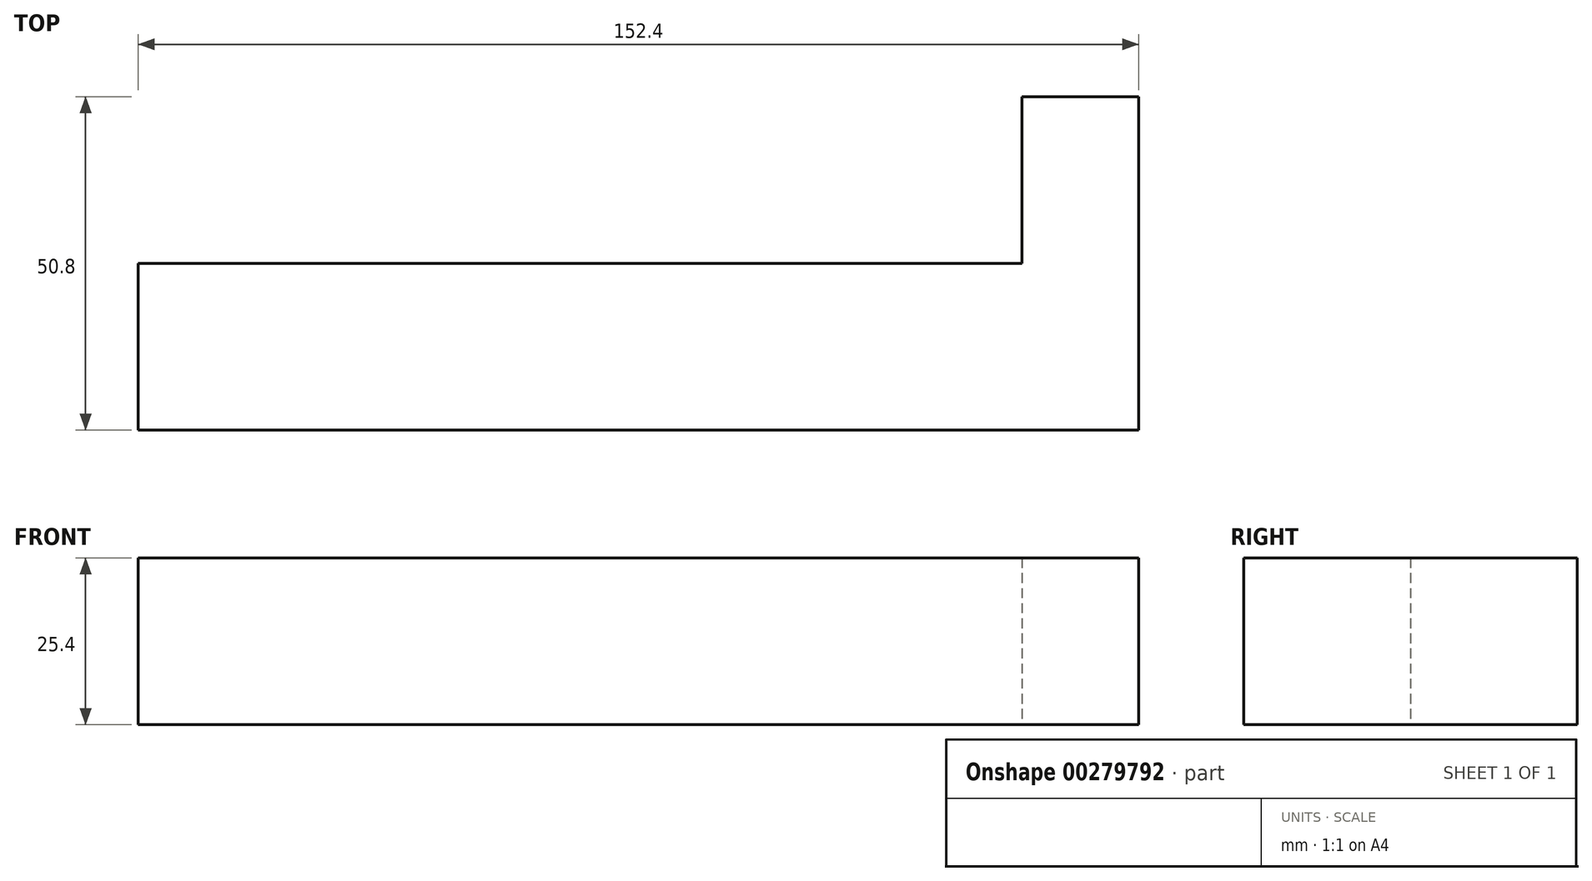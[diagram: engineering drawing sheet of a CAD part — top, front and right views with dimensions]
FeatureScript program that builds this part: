
annotation { "Feature Type Name" : "Feature", "Feature Type Description" : "" }
export const myFeature = defineFeature(function(context is Context, id is Id, definition is map)
    precondition{}
    {
        {
            var Q0;
            Q0=qCreatedBy(makeId("Right.planeOp"),FACE);
            var sketch = newSketch(context, id + "F0", { "sketchPlane" : qUnion([Q0])});
            skLineSegment(sketch, "E0.bottom", {"start": v(9.79, 30.22) * mm, "end": v(60.59, 30.22) * mm});
            skLineSegment(sketch, "E0.top", {"start": v(9.79, 4.82) * mm, "end": v(60.59, 4.82) * mm});
            skLineSegment(sketch, "E0.left", {"start": v(9.79, 30.22) * mm, "end": v(9.79, 4.82) * mm});
            skLineSegment(sketch, "E0.right", {"start": v(60.59, 30.22) * mm, "end": v(60.59, 4.82) * mm});
            skLineSegment(sketch, "E1", {"start": v(35.19, 30.22) * mm, "end": v(35.19, 4.82) * mm});
            skSolve(sketch);
        }
        {
            var Q0;
            {var subQ0=sQuery(id+"F0.wireOp",EDGE,"E0.left");Q0=makeQuery(id+"F0.imprint","IMPRINT",FACE,{"disambiguationData":[TD([[makeQuery(id+"F0.imprint","IMPRINT",EDGE,{"derivedFrom":subQ0}),1.0]])]});}
            extrude(context, id + "F1", {"entities" : qUnion([Q0]), "oppositeDirection" : true, "depth" : 152.4 * mm});
        }
        {
            var Q0;
            Q0=makeQuery(id+"F1.opExtrude","SWEPT_FACE",FACE,{"disambiguationData":[OSD([sQuery(id+"F0.wireOp",EDGE,"E1")])]});
            var sketch = newSketch(context, id + "F2", { "sketchPlane" : qUnion([Q0])});
            skLineSegment(sketch, "E2", {"start": v(17.78, 30.22) * mm, "end": v(17.78, 4.82) * mm});
            skSolve(sketch);
        }
        {
            var Q0;
            {var subQ0=sQuery(id+"F2.wireOp",EDGE,"E2");Q0=makeQuery(id+"F2.imprint","IMPRINT",FACE,{"disambiguationData":[TD([[makeQuery(id+"F2.imprint","IMPRINT",EDGE,{"derivedFrom":subQ0}),-1.0]])]});}
            extrude(context, id + "F3", {"entities" : qUnion([Q0]), "operationType" : NewBodyOperationType.ADD, "depth" : 25.4 * mm});
        }
    });
